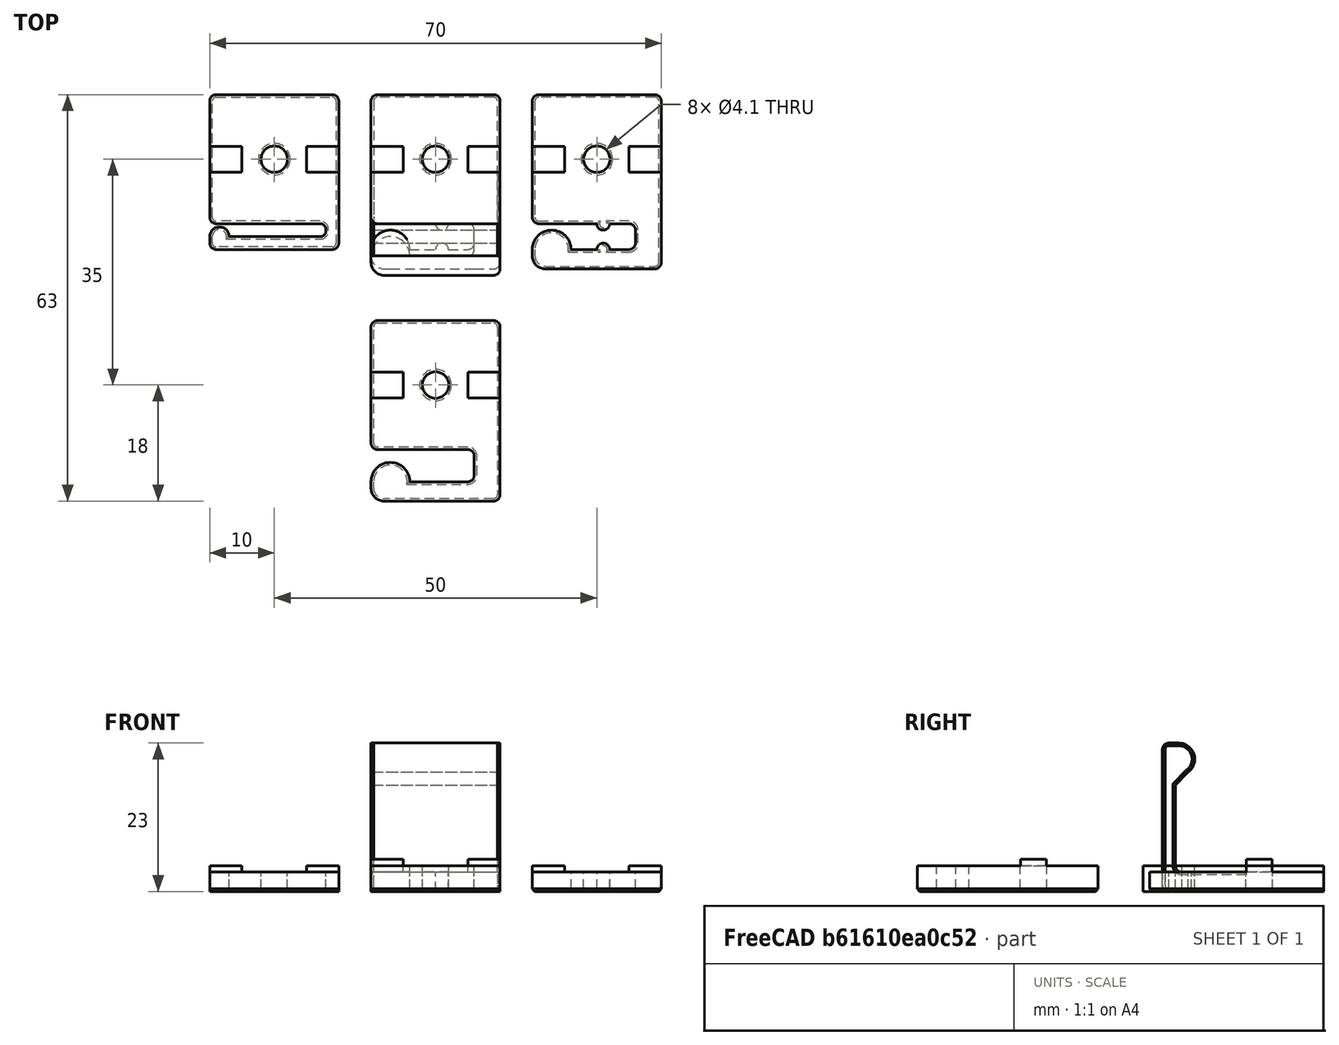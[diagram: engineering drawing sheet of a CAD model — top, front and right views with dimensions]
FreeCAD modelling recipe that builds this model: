
FCSTD DOCUMENT  (FreeCAD 0.18R14555 (Git shallow))
Label: 2020-t-slot-cable-guide
License: All rights reserved
LicenseURL: http://en.wikipedia.org/wiki/All_rights_reserved
objects: Part::Box×21, Part::Cylinder×10, Part::Fillet×7, Part::MultiFuse×5, Part::Chamfer×5, Part::Cut×4, Part::Feature×4
note: 56 computed .brp shape members not serialized (recipe doc carries the construction recipe); baked Part::Feature solids carry a one-line shape summary decoded from their .brp

FEATURE [Part::Box] Box  label="Cube"
  AttacherType = Attacher::AttachEngine3D
  Height = 3
  Length = 20
  Placement = pos=(-10,-10,0) rot=(0,0,1;0rad)
  Width = 20
FEATURE [Part::Cylinder] Cylinder
  Angle = 360
  AttacherType = Attacher::AttachEngine3D
  Height = 3
  Placement = pos=(-8.5,-12,0) rot=(0,0,1;0rad)
  Radius = 1.5
FEATURE [Part::Box] Box001  label="Cube001"
  AttacherType = Attacher::AttachEngine3D
  Height = 3
  Length = 20
  Placement = pos=(-10,-14,0) rot=(0,0,1;0rad)
  Width = 2
FEATURE [Part::Box] Box002  label="Cube002"
  AttacherType = Attacher::AttachEngine3D
  Height = 3
  Length = 2
  Placement = pos=(8,-14,0) rot=(0,0,1;0rad)
  Width = 4
FEATURE [Part::Cylinder] Cylinder001
  Angle = 360
  AttacherType = Attacher::AttachEngine3D
  Height = 10
  Radius = 2.05
FEATURE [Part::Box] Box003  label="Cube003"
  AttacherType = Attacher::AttachEngine3D
  Height = 4
  Length = 5
  Placement = pos=(5,-2,0) rot=(0,0,1;0rad)
  Width = 4
FEATURE [Part::Box] Box004  label="Cube004"
  AttacherType = Attacher::AttachEngine3D
  Height = 4
  Length = 5
  Placement = pos=(-10,-2,0) rot=(0,0,1;0rad)
  Width = 4
FEATURE [Part::MultiFuse] Fusion
  Shapes = -> [Box,Box002,Box001,Cylinder,Box003,Box004]
FEATURE [Part::Cut] Cut
  Base = -> Fusion
  Tool = -> Cylinder001
FEATURE [Part::Fillet] Fillet
  Base = -> Cut
  Edges = 5 edges r=1: [Edge4,Edge50,Edge53,Edge76,Edge88]
FEATURE [Part::Fillet] Fillet001  label="screen-cable"
  Base = -> Fillet
  Edges = 2 edges r=0.9: [Edge44,Edge72]
  Placement = pos=(-25,0,0) rot=(0,0,1;0rad)
FEATURE [Part::Box] Box005  label="Cube005"
  AttacherType = Attacher::AttachEngine3D
  Height = 3
  Length = 20
  Placement = pos=(-10,-10,0) rot=(0,0,1;0rad)
  Width = 20
FEATURE [Part::Box] Box006  label="Cube006"
  AttacherType = Attacher::AttachEngine3D
  Height = 3
  Length = 20
  Placement = pos=(-10,-17,0) rot=(0,0,1;0rad)
  Width = 3
FEATURE [Part::Box] Box007  label="Cube007"
  AttacherType = Attacher::AttachEngine3D
  Height = 3
  Length = 4
  Placement = pos=(6,-17,0) rot=(0,0,1;0rad)
  Width = 7
FEATURE [Part::Cylinder] Cylinder002
  Angle = 360
  AttacherType = Attacher::AttachEngine3D
  Height = 3
  Placement = pos=(-7,-14,0) rot=(0,0,1;0rad)
  Radius = 3
FEATURE [Part::Cylinder] Cylinder003
  Angle = 360
  AttacherType = Attacher::AttachEngine3D
  Height = 3
  Placement = pos=(1,-10,0) rot=(0,0,1;0rad)
  Radius = 1
FEATURE [Part::Cylinder] Cylinder004
  Angle = 360
  AttacherType = Attacher::AttachEngine3D
  Height = 3
  Placement = pos=(1,-14,0) rot=(0,0,1;0rad)
  Radius = 1
FEATURE [Part::Box] Box008  label="Cube008"
  AttacherType = Attacher::AttachEngine3D
  Height = 4
  Length = 5
  Placement = pos=(-10,-2,0) rot=(0,0,1;0rad)
  Width = 4
FEATURE [Part::Box] Box009  label="Cube009"
  AttacherType = Attacher::AttachEngine3D
  Height = 4
  Length = 5
  Placement = pos=(5,-2,0) rot=(0,0,1;0rad)
  Width = 4
FEATURE [Part::MultiFuse] Fusion001
  Shapes = -> [Box009,Box008,Box005,Box007,Box006,Cylinder002,Cylinder004,Cylinder003]
FEATURE [Part::Fillet] Fillet002
  Base = -> Fusion001
  Edges = 1 edges r=2: [Edge108]
FEATURE [Part::Fillet] Fillet003
  Base = -> Fillet002
  Edges = 6 edges r=1: [Edge19,Edge41,Edge53,Edge85,Edge87,Edge89]
FEATURE [Part::Cylinder] Cylinder005
  Angle = 360
  AttacherType = Attacher::AttachEngine3D
  Height = 10
  Radius = 2.05
FEATURE [Part::Cut] Cut001  label="motor-cable"
  Base = -> Fillet003
  Tool = -> Cylinder005
FEATURE [Part::Feature] Fillet001001  label="screen-cable001"
  shape: bbox 20 x 24 x 4 mm, 27 faces (baked)
FEATURE [Part::Feature] Cut001001  label="motor-cable001"
  shape: bbox 20 x 27 x 4 mm, 31 faces (baked)
FEATURE [Part::Chamfer] Chamfer
  Base = -> Fillet001001
  Edges = 16 edges r=0.4: [Edge4,Edge5,Edge9,Edge11,Edge15,Edge18,Edge24,Edge27,Edge45,Edge56,Edge59,Edge61,Edge72,Edge73,Edge74,Edge75]
FEATURE [Part::Chamfer] Chamfer001
  Base = -> Cut001001
  Edges = 21 edges r=0.4: [Edge38,Edge42,Edge43,Edge46,Edge47,Edge50,Edge54,Edge55,Edge57,Edge59,Edge60,Edge62,Edge63,Edge65,Edge68,Edge69,Edge70,Edge71,Edge72,Edge73,Edge74]
  Placement = pos=(25,0,0) rot=(0,0,1;0rad)
FEATURE [Part::Box] Box010  label="Cube010"
  AttacherType = Attacher::AttachEngine3D
  Height = 4
  Length = 20
  Placement = pos=(-10,-10,0) rot=(0,0,1;0rad)
  Width = 20
FEATURE [Part::Box] Box011  label="Cube011"
  AttacherType = Attacher::AttachEngine3D
  Height = 4
  Length = 20
  Placement = pos=(-10,-18,0) rot=(0,0,1;0rad)
  Width = 3
FEATURE [Part::Box] Box012  label="Cube012"
  AttacherType = Attacher::AttachEngine3D
  Height = 4
  Length = 4
  Placement = pos=(6,-18,0) rot=(0,0,1;0rad)
  Width = 8
FEATURE [Part::Cylinder] Cylinder006
  Angle = 360
  AttacherType = Attacher::AttachEngine3D
  Height = 4
  Placement = pos=(-7,-15,0) rot=(0,0,1;0rad)
  Radius = 3
FEATURE [Part::Box] Box013  label="Cube013"
  AttacherType = Attacher::AttachEngine3D
  Height = 5
  Length = 5
  Placement = pos=(-10,-2,0) rot=(0,0,1;0rad)
  Width = 4
FEATURE [Part::Box] Box014  label="Cube014"
  AttacherType = Attacher::AttachEngine3D
  Height = 5
  Length = 5
  Placement = pos=(5,-2,0) rot=(0,0,1;0rad)
  Width = 4
FEATURE [Part::Cylinder] Cylinder007
  Angle = 360
  AttacherType = Attacher::AttachEngine3D
  Height = 10
  Radius = 2.05
FEATURE [Part::MultiFuse] Fusion002
  Shapes = -> [Box010,Box013,Box014,Box012,Cylinder006,Box011]
FEATURE [Part::Fillet] Fillet001002
  Base = -> Fusion002
  Edges = 6 edges r=1: [Edge4,Edge32,Edge40,Edge41,Edge60,Edge73]
FEATURE [Part::Fillet] Fillet001003
  Base = -> Fillet001002
  Edges = 1 edges r=2: [Edge111]
FEATURE [Part::Cut] Cut001002
  Base = -> Fillet001003
  Tool = -> Cylinder007
FEATURE [Part::Feature] Cut001002001  label="Cut001003"
  shape: bbox 20 x 28 x 5 mm, 27 faces (baked)
FEATURE [Part::Chamfer] Chamfer002
  Base = -> Cut001002001
  Edges = 17 edges r=0.4: [Edge1,Edge37,Edge40,Edge42,Edge52,Edge56,Edge57,Edge59,Edge61,Edge64,Edge65,Edge67,Edge69,Edge72,Edge73,Edge74,Edge75]
  Placement = pos=(0,-35,0) rot=(0,0,1;0rad)
FEATURE [Part::Box] Box015  label="Cube015"
  AttacherType = Attacher::AttachEngine3D
  Height = 3
  Length = 20
  Placement = pos=(-10,-15,0) rot=(0,0,1;0rad)
  Width = 25
FEATURE [Part::Box] Box017  label="Cube017"
  AttacherType = Attacher::AttachEngine3D
  Height = 23
  Length = 20
  Placement = pos=(-10,-15,0) rot=(0,0,1;0rad)
  Width = 2
FEATURE [Part::Cylinder] Cylinder008
  Angle = 360
  AttacherType = Attacher::AttachEngine3D
  Height = 20
  Placement = pos=(10,-12.5,20.5) rot=(0,-1,0;1.5708rad)
  Radius = 2.5
FEATURE [Part::Box] Box018  label="Cube018"
  AttacherType = Attacher::AttachEngine3D
  Height = 2.5
  Length = 20
  Placement = pos=(-10,-15,20.5) rot=(0,0,1;0rad)
  Width = 2.5
FEATURE [Part::Box] Box019  label="Cube019"
  AttacherType = Attacher::AttachEngine3D
  Height = 4
  Length = 5
  Placement = pos=(-10,-2,0) rot=(0,0,1;0rad)
  Width = 4
FEATURE [Part::Box] Box020  label="Cube020"
  AttacherType = Attacher::AttachEngine3D
  Height = 4
  Length = 5
  Placement = pos=(5,-2,0) rot=(0,0,1;0rad)
  Width = 4
FEATURE [Part::Cylinder] Cylinder009
  Angle = 360
  AttacherType = Attacher::AttachEngine3D
  Height = 10
  Radius = 2.05
FEATURE [Part::MultiFuse] Fusion003
  Shapes = -> [Box020,Box017,Box015,Box018,Cylinder008,Box019]
FEATURE [Part::Fillet] Fillet001004
  Base = -> Fusion003
  Edges = 5 edges r=1: [Edge23,Edge24,Edge31,Edge43,Edge77]
FEATURE [Part::Cut] Cut001002002
  Base = -> Fillet001004
  Tool = -> Cylinder009
FEATURE [Part::Box] Box021  label="Cube021"
  AttacherType = Attacher::AttachEngine3D
  Height = 3
  Length = 20
  Placement = pos=(-10,-15,17) rot=(0,0,1;0rad)
  Width = 4
FEATURE [Part::Chamfer] Chamfer003
  Base = -> Box021
  Edges = 1 edges r=2: [Edge11]
  Placement = pos=(0,0,-0.5) rot=(0,0,1;0rad)
FEATURE [Part::MultiFuse] Fusion004
  Shapes = -> [Chamfer003,Cut001002002]
FEATURE [Part::Feature] Fusion004001  label="Fusion005"
  shape: bbox 20 x 25 x 23 mm, 24 faces (baked)
FEATURE [Part::Chamfer] Chamfer004
  Base = -> Fusion004001
  Edges = 20 edges r=0.4: [Edge1,Edge4,Edge5,Edge6,Edge8,Edge9,Edge42,Edge45,Edge47,Edge50,Edge53,Edge54,Edge55,Edge56,Edge57,Edge60,Edge63,Edge64,Edge65,Edge66]
